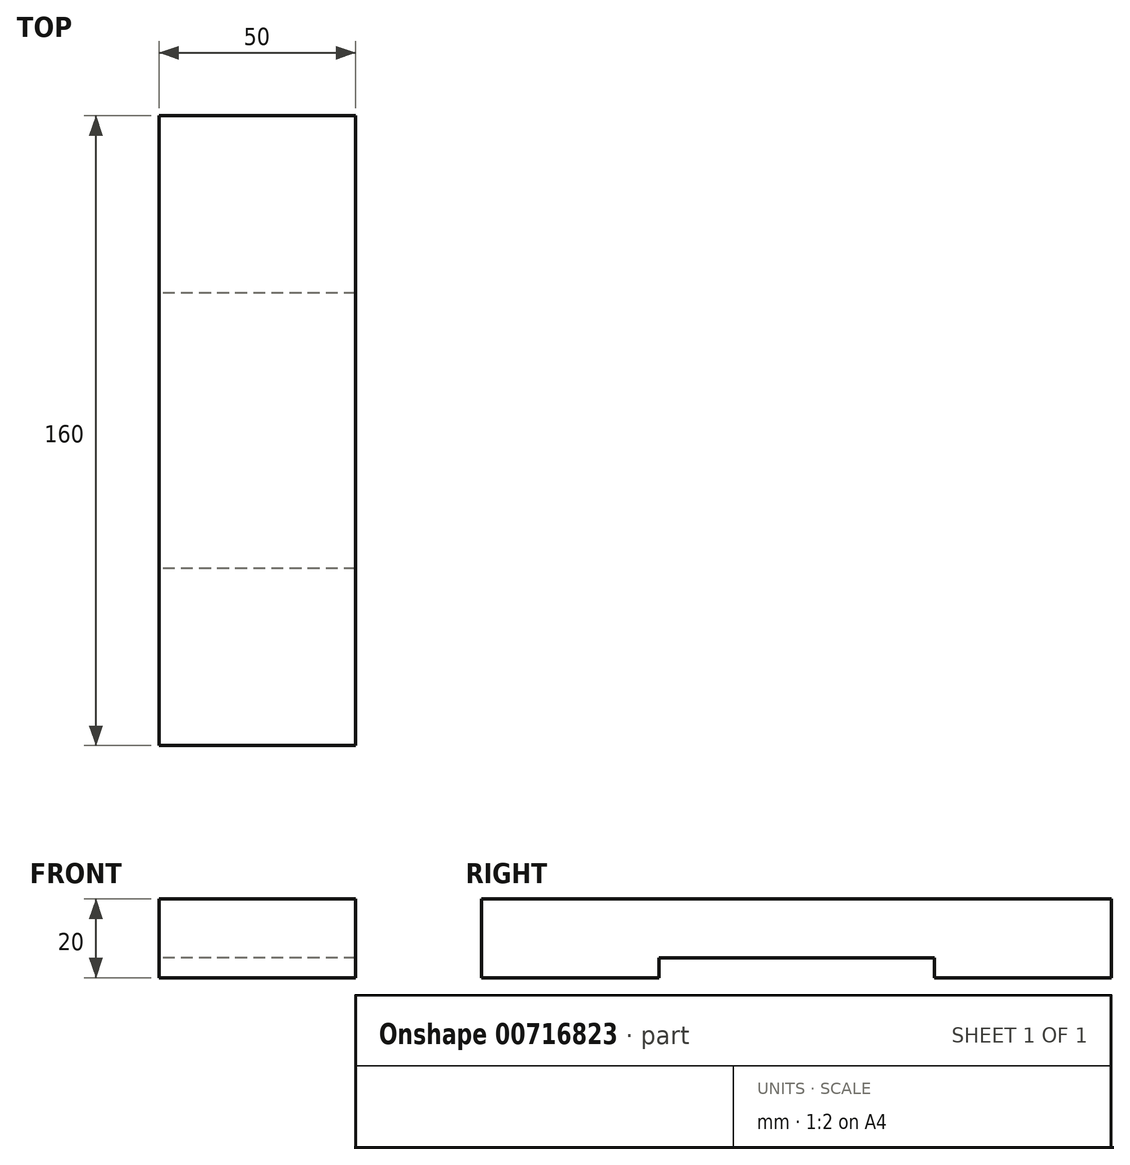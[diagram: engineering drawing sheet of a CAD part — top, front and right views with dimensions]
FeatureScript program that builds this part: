
annotation { "Feature Type Name" : "Feature", "Feature Type Description" : "" }
export const myFeature = defineFeature(function(context is Context, id is Id, definition is map)
    precondition{}
    {
        {
            var Q0;
            Q0=qCreatedBy(makeId("Front.planeOp"),FACE);
            var sketch = newSketch(context, id + "F0", { "sketchPlane" : qUnion([Q0])});
            skLineSegment(sketch, "E0.bottom", {"start": v(25, 10) * mm, "end": v(-25, 10) * mm});
            skLineSegment(sketch, "E0.top", {"start": v(25, -10) * mm, "end": v(-25, -10) * mm});
            skLineSegment(sketch, "E0.left", {"start": v(25, 10) * mm, "end": v(25, -10) * mm});
            skLineSegment(sketch, "E0.right", {"start": v(-25, 10) * mm, "end": v(-25, -10) * mm});
            skPoint(sketch, "E0.middle", {"position": v(0, 0) * mm});
            skSolve(sketch);
        }
        {
            var Q0;
            Q0 = qSketchRegion(id + "F0", true);
            extrude(context, id + "F1", {"entities" : qUnion([Q0]), "endBound" : BoundingType.SYMMETRIC, "depth" : 160 * mm, "offsetDistance" : 25 * mm});
        }
        {
            var Q0;
            Q0=makeQuery(id+"F1.opExtrude","SWEPT_FACE",FACE,{"disambiguationData":[OSD([sQuery(id+"F0.wireOp",EDGE,"E0.top")])]});
            var sketch = newSketch(context, id + "F2", { "sketchPlane" : qUnion([Q0])});
            skLineSegment(sketch, "E1.bottom", {"start": v(25, 35) * mm, "end": v(-25, 35) * mm});
            skLineSegment(sketch, "E1.top", {"start": v(25, -35) * mm, "end": v(-25, -35) * mm});
            skLineSegment(sketch, "E1.left", {"start": v(25, 35) * mm, "end": v(25, -35) * mm});
            skLineSegment(sketch, "E1.right", {"start": v(-25, 35) * mm, "end": v(-25, -35) * mm});
            skPoint(sketch, "E1.middle", {"position": v(0, 0) * mm});
            skSolve(sketch);
        }
        {
            var Q0;
            Q0 = qSketchRegion(id + "F2", true);
            extrude(context, id + "F3", {"entities" : qUnion([Q0]), "operationType" : NewBodyOperationType.REMOVE, "oppositeDirection" : true, "depth" : 5 * mm, "offsetDistance" : 25 * mm});
        }
    });
